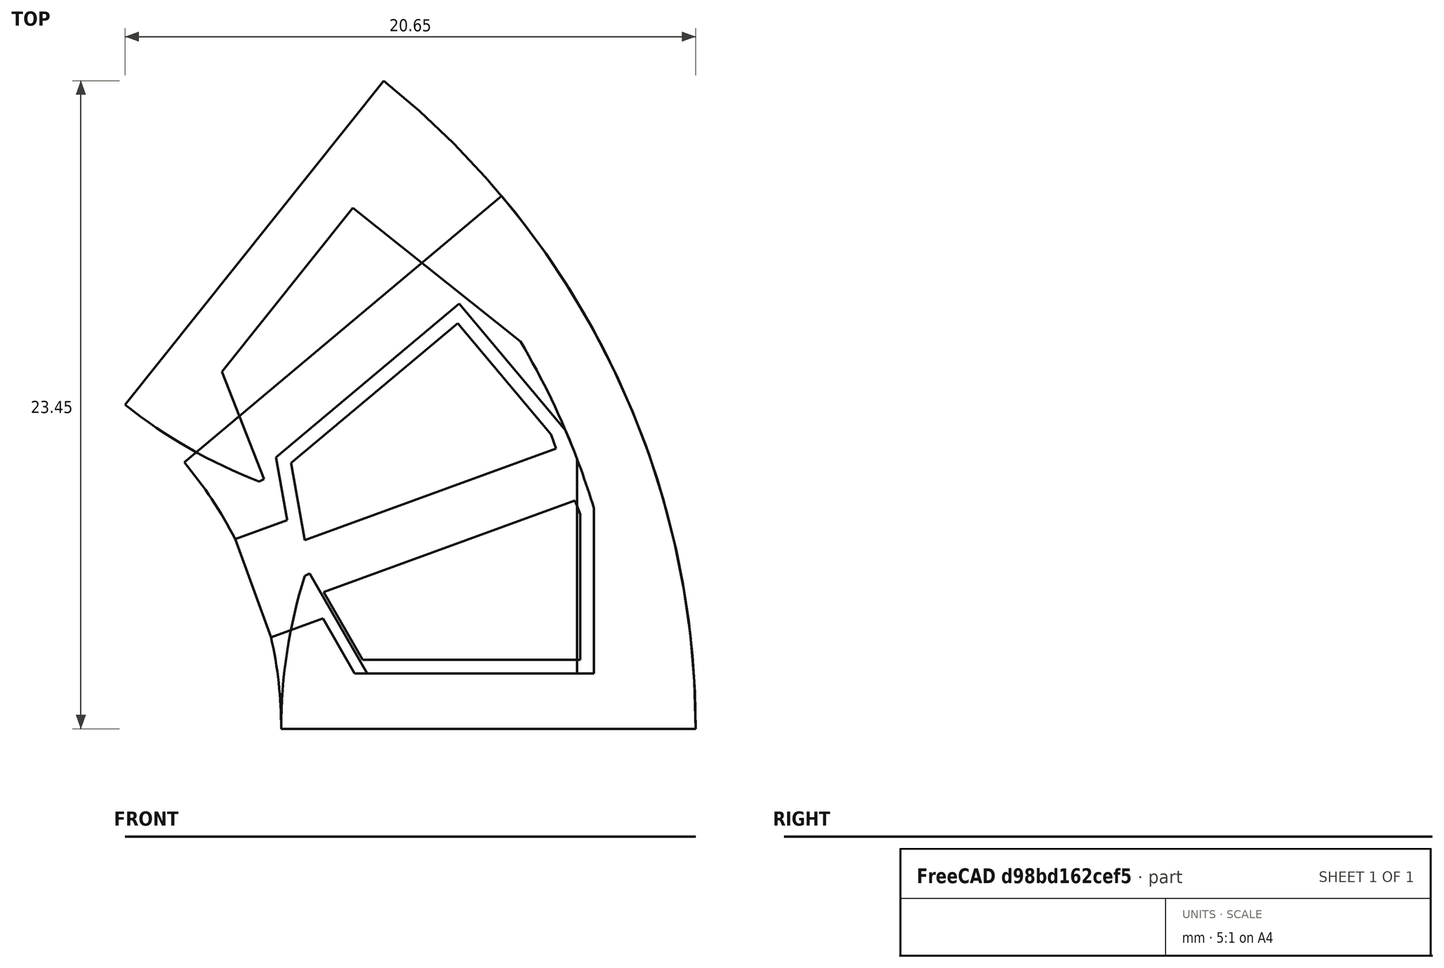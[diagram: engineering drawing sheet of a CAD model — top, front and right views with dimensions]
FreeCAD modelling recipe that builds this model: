
FCSTD DOCUMENT  (FreeCAD 0.18R4 (GitTag))
Label: StatorIRNeedleWinding
License: All rights reserved
LicenseURL: http://en.wikipedia.org/wiki/All_rights_reserved
objects: Sketcher::SketchObject×9, Surface::Filling×5, PartDesign::Body×2, Spreadsheet::Sheet×1
note: 16 computed .brp shape members not serialized (recipe doc carries the construction recipe); baked Part::Feature solids carry a one-line shape summary decoded from their .brp

FEATURE [Spreadsheet::Sheet] Spreadsheet  label="Variables"
  cells = A2=slotNumber; B2(slotNumber)=9; A3=outerDiameter; B3(outerDiameter)=60; A4=innerDiameter; B4(innerDiameter)=30; A5=stackLength; B5(stackLength)=20; A6=stackingFactor; B6(stackingFactor)=0.95; A7=cuttingThickness; B7(cuttingThickness)=0.1; A8=skewAngle; B8(skewAngle)=0; A9=segmentAngle; B9(segmentAngle)==360 / slotNumber; A10=tipHeightReduction; B10(tipHeightReduction)=0; A11=toothThickness; B11(toothThickness)=4; A12=yokeThickness; B12(yokeThickness)=2.5; A13=tipHeight; B13(tipHeight)=2; A14=tipAngle; B14(tipAngle)=120; A15=openingLeft; B15(openingLeft)=1.9; A16=openingRight; B16(openingRight)=1.9; A17=slotIsolation; B17(slotIsolation)=0.5; A18=windingAngle; B18(windingAngle)=35; A19=heightRatio; B19(heightRatio)=45; A20=roundingRadii; B20(roundingRadii)=0.2; A21=backWidth; B21(backWidth)=3; A22=backAngle; B22(backAngle)=90; A23=phaseSeparation; B23(phaseSeparation)=2; A24=axialOverhang; B24(axialOverhang)=1.2; A25=axialHeight; B25(axialHeight)=3
FEATURE [Sketcher::SketchObject] Sketch003  label="StatorSketch1"
  MapMode = 5
  Support = -> [XY_Plane]
  expr: Constraints[76] = Variables.backWidth
  expr: Constraints[37] = Variables.tipAngle
  expr: Constraints[60] = Variables.backAngle
  expr: Constraints[30] = Variables.tipHeight
  expr: Constraints[28] = Variables.openingRight
  expr: Constraints[32] = Variables.tipHeight * (1 - Variables.tipHeightReduction / 100)
  expr: Constraints[22] = Variables.openingLeft
  expr: Constraints[6] = Variables.outerDiameter / 2
  expr: Constraints[59] = Variables.tipHeight
  expr: Constraints[5] = Variables.segmentAngle
  expr: Constraints[11] = Variables.innerDiameter / 2
  expr: Constraints[54] = Variables.outerDiameter / 2 - Variables.yokeThickness
  expr: Constraints[49] = Variables.tipHeight * (1 - Variables.tipHeightReduction / 100)
  expr: Constraints[58] = Variables.toothThickness / 2
  expr: Constraints[18] = Variables.segmentAngle / 2
  expr: Constraints[50] = Variables.tipAngle
  expr: Constraints[52] = Variables.backAngle
  expr: Constraints[42] = Variables.toothThickness / 2
  sketch-geometry (27):
    g0: LineSegment [constr] StartX=0 StartY=0 StartZ=0 EndX=22.9813 EndY=19.2836 EndZ=0
    g1: LineSegment [constr] StartX=0 StartY=0 StartZ=0 EndX=30 EndY=0 EndZ=0
    g2: ArcOfCircle CenterX=0 CenterY=0 CenterZ=0 NormalX=0 NormalY=0 NormalZ=1 AngleXU=0 Radius=30 StartAngle=0 EndAngle=0.698132
    g3: ArcOfCircle [constr] CenterX=0 CenterY=0 CenterZ=0 NormalX=0 NormalY=0 NormalZ=1 AngleXU=0 Radius=15 StartAngle=0 EndAngle=0.698132
    g4: LineSegment [constr] StartX=13.3338 StartY=6.87098 StartZ=0 EndX=27.4859 EndY=12.0219 EndZ=0
    g5: LineSegment [constr] StartX=14.6308 StartY=3.30731 StartZ=0 EndX=28.7829 EndY=8.45826 EndZ=0
    g6: LineSegment [constr] StartX=28.1908 StartY=10.2606 StartZ=0 EndX=14.0954 EndY=5.1303 EndZ=0
    g7: LineSegment [constr] StartX=0 StartY=0 StartZ=0 EndX=14.0954 EndY=5.1303 EndZ=0
    g8: LineSegment [constr] StartX=13.3338 StartY=6.87098 StartZ=0 EndX=14.0954 EndY=5.1303 EndZ=0
    g9: LineSegment [constr] StartX=14.0954 StartY=5.1303 StartZ=0 EndX=14.6308 EndY=3.30731 EndZ=0
    g10: LineSegment [constr] StartX=13.3338 StartY=6.87098 StartZ=0 EndX=15.2132 EndY=7.55502 EndZ=0
    g11: LineSegment StartX=13.3338 StartY=6.87098 StartZ=0 EndX=15.2132 EndY=7.55502 EndZ=0
    g12: LineSegment StartX=15.2132 StartY=7.55502 StartZ=0 EndX=14.8139 EndY=9.8195 EndZ=0
    g13: LineSegment StartX=14.8139 StartY=9.8195 StartZ=0 EndX=21.4449 EndY=15.3836 EndZ=0
    g14: LineSegment [constr] StartX=14.8139 StartY=9.8195 StartZ=0 EndX=13.5283 EndY=11.3516 EndZ=0
    g15: LineSegment StartX=21.4449 StartY=15.3836 StartZ=0 EndX=25.29 EndY=10.8011 EndZ=0
    g16: LineSegment StartX=26.3161 StartY=7.98201 StartZ=0 EndX=26.3161 EndY=2 EndZ=0
    g17: LineSegment StartX=26.3161 StartY=2 StartZ=0 EndX=17.6599 EndY=2 EndZ=0
    g18: LineSegment StartX=17.6599 StartY=2 StartZ=0 EndX=16.5102 EndY=3.99135 EndZ=0
    g19: LineSegment StartX=16.5102 StartY=3.99135 StartZ=0 EndX=14.6308 EndY=3.30731 EndZ=0
    g20: LineSegment [constr] StartX=26.3161 StartY=2 StartZ=0 EndX=26.3161 EndY=0 EndZ=0
    g21: LineSegment StartX=11.4907 StartY=9.64181 StartZ=0 EndX=22.9813 EndY=19.2836 EndZ=0
    g22: LineSegment StartX=30 StartY=0 StartZ=0 EndX=15 EndY=0 EndZ=0
    g23: ArcOfCircle CenterX=4.23e-14 CenterY=0 CenterZ=0 NormalX=0 NormalY=0 NormalZ=1 AngleXU=0 Radius=15 StartAngle=0 EndAngle=0.222314
    g24: ArcOfCircle CenterX=-4.12e-14 CenterY=-3.45e-14 CenterZ=0 NormalX=0 NormalY=0 NormalZ=1 AngleXU=0 Radius=15 StartAngle=0.475817 EndAngle=0.698132
    g25: ArcOfCircle CenterX=0 CenterY=0 CenterZ=0 NormalX=0 NormalY=0 NormalZ=1 AngleXU=0 Radius=27.5 StartAngle=0.294493 EndAngle=0.403638
    g26: LineSegment [constr] StartX=25.29 StartY=10.8011 StartZ=0 EndX=26.3161 EndY=7.98201 EndZ=0
  constraints (77):
    c: Angle(g-1,g1) = 0
    c: Coincident(g0,g-1)
    c: Coincident(g1,g-1)
    c: Coincident(g2,g-1)
    c: Coincident(g2,g0)
    c: Angle(g1,g0) = 0.698132
    c: Radius(g2) = 30
    c: Coincident(g2,g1)
    c: Coincident(g3,g-1)
    c: PointOnObject(g3,g1)
    c: PointOnObject(g3,g0)
    c: Radius(g3) = 15
    c: PointOnObject(g4,g3)
    c: PointOnObject(g4,g2)
    c: PointOnObject(g5,g3)
    c: PointOnObject(g5,g2)
    c: PointOnObject(g6,g2)
    c: PointOnObject(g6,g3)
    c: Angle(g1,g6) = 0.349066
    c: Coincident(g7,g-1)
    c: Coincident(g7,g6)
    c: Coincident(g8,g4)
    c: Distance(g8) = 1.9
    c: Coincident(g8,g6)
    c: Parallel(g4,g6)
    c: Parallel(g5,g6)
    c: Coincident(g9,g6)
    c: Coincident(g9,g5)
    c: Distance(g9) = 1.9
    c: PointOnObject(g10,g4)
    c: Distance(g4,g10) = 2
    c: Angle(g4,g10) = 3.14159
    c: Distance(g10,g10) = 2
    c: Coincident(g11,g10)
    c: Coincident(g12,g11)
    c: Coincident(g13,g12)
    c: Coincident(g11,g10)
    c: Angle(g12,g13) = 2.0944
    c: Parallel(g0,g13)
    c: Coincident(g14,g12)
    c: PointOnObject(g14,g0)
    c: Angle(g13,g14) = 1.5708
    c: Distance(g14) = 2
    c: Coincident(g15,g13)
    c: Coincident(g17,g16)
    c: Coincident(g18,g17)
    c: PointOnObject(g18,g5)
    c: Coincident(g19,g18)
    c: PointOnObject(g19,g5)
    c: Distance(g19) = 2
    c: Angle(g17,g18) = 2.0944
    c: Parallel(g17,g1)
    c: Angle(g16,g17) = 1.5708
    c: Symmetric(g15,g16,g6)
    c: Distance(g-1,g15) = 27.5
    c: Coincident(g20,g16)
    c: PointOnObject(g20,g1)
    c: Vertical(g20)
    c: DistanceY(g20,g20) = 2
    c: Distance(g5,g18) = 2
    c: Angle(g13,g15) = 1.5708
    c: Coincident(g21,g3)
    c: Coincident(g21,g0)
    c: Coincident(g22,g2)
    c: Coincident(g22,g3)
    c: PointOnObject(g23,g-1)
    c: Coincident(g23,g19)
    c: Coincident(g23,g22)
    c: PointOnObject(g24,g0)
    c: Coincident(g24,g11)
    c: Coincident(g24,g21)
    c: Coincident(g25,g2)
    c: Coincident(g25,g15)
    c: Coincident(g25,g16)
    c: Coincident(g26,g15)
    c: Coincident(g26,g16)
    c: Distance(g26) = 3
FEATURE [Sketcher::SketchObject] Sketch  label="StatorStack"
  MapMode = 5
  Support = -> [XY_Plane001]
  expr: Constraints[20] = Variables.innerDiameter / 2
  expr: Constraints[10] = Variables.outerDiameter / 2
  expr: Constraints[9] = Variables.innerDiameter / 2
  expr: Constraints[8] = Variables.stackLength
  sketch-geometry (8):
    g0: LineSegment StartX=-10 StartY=15 StartZ=0 EndX=10 EndY=15 EndZ=0
    g1: LineSegment StartX=10 StartY=15 StartZ=0 EndX=10 EndY=30 EndZ=0
    g2: LineSegment StartX=10 StartY=30 StartZ=0 EndX=-10 EndY=30 EndZ=0
    g3: LineSegment StartX=-10 StartY=30 StartZ=0 EndX=-10 EndY=15 EndZ=0
    g4: LineSegment StartX=-10 StartY=-15 StartZ=0 EndX=10 EndY=-15 EndZ=0
    g5: LineSegment StartX=10 StartY=-15 StartZ=0 EndX=10 EndY=-30 EndZ=0
    g6: LineSegment StartX=10 StartY=-30 StartZ=0 EndX=-10 EndY=-30 EndZ=0
    g7: LineSegment StartX=-10 StartY=-30 StartZ=0 EndX=-10 EndY=-15 EndZ=0
  constraints (22):
    c: Coincident(g0,g1)
    c: Coincident(g1,g2)
    c: Coincident(g2,g3)
    c: Coincident(g3,g0)
    c: Horizontal(g2)
    c: Vertical(g1)
    c: Vertical(g3)
    c: Symmetric(g0,g0,g-2)
    c: DistanceX(g0,g0) = 20
    c: DistanceY(g-1,g0) = 15
    c: DistanceY(g-1,g1) = 30
    c: Coincident(g4,g5)
    c: Coincident(g5,g6)
    c: Coincident(g6,g7)
    c: Coincident(g7,g4)
    c: Horizontal(g6)
    c: Vertical(g5)
    c: Vertical(g7)
    c: Equal(g4,g0)
    c: Symmetric(g4,g4,g-2)
    c: DistanceY(g4,g-1) = 15
    c: Equal(g7,g3)
FEATURE [Sketcher::SketchObject] Sketch005  label="StatorSketch2"
  MapMode = 5
  Support = -> [XY_Plane]
  expr: Constraints[76] = Variables.backWidth
  expr: Constraints[51] = Variables.tipAngle
  expr: Constraints[28] = Variables.openingRight
  expr: Constraints[30] = Variables.tipHeight
  expr: Constraints[37] = Variables.tipAngle
  expr: Constraints[60] = Variables.tipHeight
  expr: Constraints[32] = Variables.tipHeight * (1 - Variables.tipHeightReduction / 100)
  expr: Constraints[61] = Variables.backAngle
  expr: Constraints[6] = Variables.outerDiameter / 2
  expr: Constraints[5] = Variables.segmentAngle
  expr: Constraints[22] = Variables.openingLeft
  expr: Constraints[55] = Variables.outerDiameter / 2 - Variables.yokeThickness
  expr: Constraints[59] = Variables.toothThickness / 2
  expr: Constraints[50] = Variables.tipHeight * (1 - Variables.tipHeightReduction / 100)
  expr: Constraints[18] = Variables.segmentAngle / 2
  expr: Constraints[11] = Variables.innerDiameter / 2
  expr: Constraints[53] = Variables.backAngle
  expr: Constraints[42] = Variables.toothThickness / 2
  sketch-geometry (27):
    g0: LineSegment [constr] StartX=0 StartY=0 StartZ=0 EndX=18.7047 EndY=23.4549 EndZ=0
    g1: LineSegment [constr] StartX=0 StartY=0 StartZ=0 EndX=30 EndY=0 EndZ=0
    g2: ArcOfCircle CenterX=0 CenterY=0 CenterZ=0 NormalX=0 NormalY=0 NormalZ=1 AngleXU=0 Radius=30 StartAngle=0 EndAngle=0.897598
    g3: ArcOfCircle [constr] CenterX=0 CenterY=0 CenterZ=0 NormalX=0 NormalY=0 NormalZ=1 AngleXU=0 Radius=15 StartAngle=0 EndAngle=0.897598
    g4: LineSegment [constr] StartX=12.5834 StartY=8.16445 StartZ=0 EndX=26.1523 EndY=14.6989 EndZ=0
    g5: LineSegment [constr] StartX=14.2288 StartY=4.74764 StartZ=0 EndX=27.7977 EndY=11.2821 EndZ=0
    g6: LineSegment [constr] StartX=27.0291 StartY=13.0165 StartZ=0 EndX=13.5145 EndY=6.50826 EndZ=0
    g7: LineSegment [constr] StartX=0 StartY=0 StartZ=0 EndX=13.5145 EndY=6.50826 EndZ=0
    g8: LineSegment [constr] StartX=12.5834 StartY=8.16445 StartZ=0 EndX=13.5145 EndY=6.50826 EndZ=0
    g9: LineSegment [constr] StartX=13.5145 StartY=6.50826 StartZ=0 EndX=14.2288 EndY=4.74764 EndZ=0
    g10: LineSegment [constr] StartX=14.2051 StartY=8.94544 StartZ=0 EndX=14.3853 EndY=9.03222 EndZ=0
    g11: LineSegment StartX=14.2051 StartY=8.94544 StartZ=0 EndX=14.3853 EndY=9.03222 EndZ=0
    g12: LineSegment StartX=14.3853 StartY=9.03222 StartZ=0 EndX=12.8601 EndY=12.9183 EndZ=0
    g13: LineSegment StartX=12.8601 StartY=12.9183 StartZ=0 EndX=17.5931 EndY=18.8533 EndZ=0
    g14: LineSegment [constr] StartX=12.8601 StartY=12.9183 StartZ=0 EndX=11.2965 EndY=14.1653 EndZ=0
    g15: LineSegment StartX=17.5931 StartY=18.8533 StartZ=0 EndX=23.6613 EndY=14.0141 EndZ=0
    g16: LineSegment [constr] StartX=23.6613 StartY=14.0141 StartZ=0 EndX=25.7092 EndY=9.7615 EndZ=0
    g17: LineSegment StartX=25.7092 StartY=9.7615 StartZ=0 EndX=25.7092 EndY=2 EndZ=0
    g18: LineSegment StartX=25.7092 StartY=2 StartZ=0 EndX=18.1181 EndY=2 EndZ=0
    g19: LineSegment StartX=18.1181 StartY=2 StartZ=0 EndX=16.0308 EndY=5.61541 EndZ=0
    g20: LineSegment StartX=16.0308 StartY=5.61541 StartZ=0 EndX=15.8506 EndY=5.52863 EndZ=0
    g21: LineSegment [constr] StartX=25.7092 StartY=2 StartZ=0 EndX=25.7092 EndY=0 EndZ=0
    g22: LineSegment StartX=9.35235 StartY=11.7275 StartZ=0 EndX=18.7047 EndY=23.4549 EndZ=0
    g23: LineSegment StartX=30 StartY=0 StartZ=0 EndX=15 EndY=0 EndZ=0
    g24: ArcOfCircle CenterX=20.8201 CenterY=26.1075 CenterZ=0 NormalX=0 NormalY=0 NormalZ=1 AngleXU=0 Radius=18.3928 StartAngle=4.03919 EndAngle=4.3445
    g25: ArcOfCircle CenterX=33.3928 CenterY=0 CenterZ=0 NormalX=0 NormalY=0 NormalZ=1 AngleXU=0 Radius=18.3928 StartAngle=2.83628 EndAngle=3.14159
    g26: ArcOfCircle CenterX=0 CenterY=0 CenterZ=0 NormalX=0 NormalY=0 NormalZ=1 AngleXU=0 Radius=27.5 StartAngle=0.362875 EndAngle=0.534723
  constraints (77):
    c: Angle(g-1,g1) = 0
    c: Coincident(g0,g-1)
    c: Coincident(g1,g-1)
    c: Coincident(g2,g-1)
    c: Coincident(g2,g0)
    c: Angle(g1,g0) = 0.698132
    c: Radius(g2) = 30
    c: Coincident(g2,g1)
    c: Coincident(g3,g-1)
    c: PointOnObject(g3,g1)
    c: PointOnObject(g3,g0)
    c: Radius(g3) = 15
    c: PointOnObject(g4,g3)
    c: PointOnObject(g4,g2)
    c: PointOnObject(g5,g3)
    c: PointOnObject(g5,g2)
    c: PointOnObject(g6,g2)
    c: PointOnObject(g6,g3)
    c: Angle(g1,g6) = 0.349066
    c: Coincident(g7,g-1)
    c: Coincident(g7,g6)
    c: Coincident(g8,g4)
    c: Distance(g8) = 1.9
    c: Coincident(g8,g6)
    c: Parallel(g4,g6)
    c: Parallel(g5,g6)
    c: Coincident(g9,g6)
    c: Coincident(g9,g5)
    c: Distance(g9) = 1.9
    c: PointOnObject(g10,g4)
    c: Distance(g4,g10) = 2
    c: Angle(g4,g10) = 3.14159
    c: Distance(g10,g10) = 2
    c: Coincident(g11,g10)
    c: Coincident(g12,g11)
    c: Coincident(g13,g12)
    c: Coincident(g11,g10)
    c: Angle(g12,g13) = 2.0944
    c: Parallel(g0,g13)
    c: Coincident(g14,g12)
    c: PointOnObject(g14,g0)
    c: Angle(g13,g14) = 1.5708
    c: Distance(g14) = 2
    c: Coincident(g15,g13)
    c: Coincident(g16,g15)
    c: Coincident(g17,g16)
    c: Coincident(g18,g17)
    c: Coincident(g19,g18)
    c: PointOnObject(g19,g5)
    c: Coincident(g20,g19)
    c: Distance(g20) = 2
    c: Angle(g18,g19) = 2.0944
    c: Parallel(g18,g1)
    c: Angle(g17,g18) = 1.5708
    c: Symmetric(g15,g16,g6)
    c: Distance(g-1,g15) = 27.5
    c: Coincident(g21,g17)
    c: PointOnObject(g21,g1)
    c: Vertical(g21)
    c: DistanceY(g21,g21) = 2
    c: Distance(g5,g19) = 2
    c: Angle(g13,g15) = 1.5708
    c: Coincident(g22,g3)
    c: Coincident(g22,g0)
    c: Coincident(g23,g2)
    c: Coincident(g23,g3)
    c: PointOnObject(g24,g22)
    c: Coincident(g24,g11)
    c: Coincident(g24,g22)
    c: Angle(g5,g20) = 3.14159
    c: PointOnObject(g25,g-1)
    c: Coincident(g25,g20)
    c: Coincident(g25,g23)
    c: Coincident(g26,g2)
    c: Coincident(g26,g15)
    c: Coincident(g26,g17)
    c: Distance(g16) = 3
FEATURE [Sketcher::SketchObject] Sketch008  label="SlotSketch"
  MapMode = 5
  Support = -> [XY_Plane]
  expr: Constraints[50] = Variables.toothThickness / 2
  expr: Constraints[18] = Variables.segmentAngle / 2
  expr: Constraints[30] = Variables.tipAngle
  expr: Constraints[51] = Variables.tipHeight
  expr: Constraints[28] = Variables.openingRight
  expr: Constraints[67] = Variables.backWidth
  expr: Constraints[46] = Variables.outerDiameter / 2 - Variables.yokeThickness
  expr: Constraints[22] = Variables.openingLeft
  expr: Constraints[6] = Variables.outerDiameter / 2
  expr: Constraints[44] = Variables.backAngle
  expr: Constraints[52] = Variables.backAngle
  expr: Constraints[11] = Variables.innerDiameter / 2
  expr: Constraints[5] = Variables.segmentAngle
  expr: Constraints[42] = Variables.tipAngle
  expr: Constraints[35] = Variables.toothThickness / 2
  sketch-geometry (25):
    g0: LineSegment [constr] StartX=0 StartY=0 StartZ=0 EndX=22.9813 EndY=19.2836 EndZ=0
    g1: LineSegment [constr] StartX=0 StartY=0 StartZ=0 EndX=30 EndY=0 EndZ=0
    g2: ArcOfCircle [constr] CenterX=0 CenterY=0 CenterZ=0 NormalX=0 NormalY=0 NormalZ=1 AngleXU=0 Radius=30 StartAngle=0 EndAngle=0.698132
    g3: ArcOfCircle [constr] CenterX=0 CenterY=0 CenterZ=0 NormalX=0 NormalY=0 NormalZ=1 AngleXU=0 Radius=15 StartAngle=0 EndAngle=0.698132
    g4: LineSegment [constr] StartX=13.3338 StartY=6.87098 StartZ=0 EndX=27.4859 EndY=12.0219 EndZ=0
    g5: LineSegment [constr] StartX=14.6308 StartY=3.30731 StartZ=0 EndX=28.7829 EndY=8.45826 EndZ=0
    g6: LineSegment [constr] StartX=28.1908 StartY=10.2606 StartZ=0 EndX=14.0954 EndY=5.1303 EndZ=0
    g7: LineSegment [constr] StartX=0 StartY=0 StartZ=0 EndX=14.0954 EndY=5.1303 EndZ=0
    g8: LineSegment [constr] StartX=13.3338 StartY=6.87098 StartZ=0 EndX=14.0954 EndY=5.1303 EndZ=0
    g9: LineSegment [constr] StartX=14.0954 StartY=5.1303 StartZ=0 EndX=14.6308 EndY=3.30731 EndZ=0
    g10: LineSegment StartX=15.2132 StartY=7.55502 StartZ=0 EndX=14.8139 EndY=9.8195 EndZ=0
    g11: LineSegment StartX=14.8139 StartY=9.8195 StartZ=0 EndX=21.4449 EndY=15.3836 EndZ=0
    g12: LineSegment [constr] StartX=14.8139 StartY=9.8195 StartZ=0 EndX=13.5283 EndY=11.3516 EndZ=0
    g13: LineSegment StartX=21.4449 StartY=15.3836 StartZ=0 EndX=25.29 EndY=10.8011 EndZ=0
    g14: LineSegment [constr] StartX=25.29 StartY=10.8011 StartZ=0 EndX=26.3161 EndY=7.98201 EndZ=0
    g15: LineSegment StartX=26.3161 StartY=7.98201 StartZ=0 EndX=26.3161 EndY=2 EndZ=0
    g16: LineSegment StartX=26.3161 StartY=2 StartZ=0 EndX=17.6599 EndY=2 EndZ=0
    g17: LineSegment StartX=17.6599 StartY=2 StartZ=0 EndX=16.5102 EndY=3.99135 EndZ=0
    g18: LineSegment [constr] StartX=26.3161 StartY=2 StartZ=0 EndX=26.3161 EndY=0 EndZ=0
    g19: LineSegment [constr] StartX=11.4907 StartY=9.64181 StartZ=0 EndX=22.9813 EndY=19.2836 EndZ=0
    g20: LineSegment [constr] StartX=30 StartY=0 StartZ=0 EndX=15 EndY=0 EndZ=0
    g21: LineSegment StartX=13.3338 StartY=6.87098 StartZ=0 EndX=14.6308 EndY=3.30731 EndZ=0
    g22: LineSegment StartX=13.3338 StartY=6.87098 StartZ=0 EndX=15.2132 EndY=7.55502 EndZ=0
    g23: LineSegment StartX=14.6308 StartY=3.30731 StartZ=0 EndX=16.5102 EndY=3.99135 EndZ=0
    g24: ArcOfCircle CenterX=0 CenterY=0 CenterZ=0 NormalX=0 NormalY=0 NormalZ=1 AngleXU=0 Radius=27.5 StartAngle=0.294493 EndAngle=0.403638
  constraints (68):
    c: Angle(g-1,g1) = 0
    c: Coincident(g0,g-1)
    c: Coincident(g1,g-1)
    c: Coincident(g2,g-1)
    c: Coincident(g2,g0)
    c: Angle(g1,g0) = 0.698132
    c: Radius(g2) = 30
    c: Coincident(g2,g1)
    c: Coincident(g3,g-1)
    c: PointOnObject(g3,g1)
    c: PointOnObject(g3,g0)
    c: Radius(g3) = 15
    c: PointOnObject(g4,g3)
    c: PointOnObject(g4,g2)
    c: PointOnObject(g5,g3)
    c: PointOnObject(g5,g2)
    c: PointOnObject(g6,g2)
    c: PointOnObject(g6,g3)
    c: Angle(g1,g6) = 0.349066
    c: Coincident(g7,g-1)
    c: Coincident(g7,g6)
    c: Coincident(g8,g4)
    c: Distance(g8) = 1.9
    c: Coincident(g8,g6)
    c: Parallel(g4,g6)
    c: Parallel(g5,g6)
    c: Coincident(g9,g6)
    c: Coincident(g9,g5)
    c: Distance(g9) = 1.9
    c: Coincident(g11,g10)
    c: Angle(g10,g11) = 2.0944
    c: Parallel(g0,g11)
    c: Coincident(g12,g10)
    c: PointOnObject(g12,g0)
    c: Angle(g11,g12) = 1.5708
    c: Distance(g12) = 2
    c: Coincident(g13,g11)
    c: Coincident(g14,g13)
    c: Coincident(g15,g14)
    c: Coincident(g16,g15)
    c: Coincident(g17,g16)
    c: PointOnObject(g17,g5)
    c: Angle(g16,g17) = 2.0944
    c: Parallel(g16,g1)
    c: Angle(g15,g16) = 1.5708
    c: Symmetric(g13,g14,g6)
    c: Distance(g-1,g13) = 27.5
    c: Coincident(g18,g15)
    c: PointOnObject(g18,g1)
    c: Vertical(g18)
    c: DistanceY(g18,g18) = 2
    c: Distance(g5,g17) = 2
    c: Angle(g11,g13) = 1.5708
    c: Coincident(g19,g3)
    c: Coincident(g19,g0)
    c: Coincident(g20,g2)
    c: Coincident(g20,g3)
    c: Symmetric(g17,g10,g6)
    c: Coincident(g21,g4)
    c: Coincident(g21,g5)
    c: Coincident(g22,g21)
    c: Coincident(g22,g10)
    c: Coincident(g23,g21)
    c: Coincident(g23,g17)
    c: Coincident(g24,g-1)
    c: Coincident(g24,g13)
    c: Coincident(g24,g15)
    c: Distance(g14) = 3
FEATURE [Sketcher::SketchObject] Sketch006  label="TerminalLeftSketch"
  ExternalGeometry = -> [Sketch008]
  MapMode = 5
  Support = -> [XY_Plane]
  expr: Constraints[28] = abs(Variables.backWidth - Variables.phaseSeparation) / 2 + Variables.slotIsolation / 15
  expr: Constraints[21] = Variables.slotIsolation
  expr: Constraints[14] = Variables.phaseSeparation / 2
  sketch-geometry (10):
    g0: LineSegment StartX=24.7672 StartY=10.6463 StartZ=0 EndX=21.3833 EndY=14.6792 EndZ=0
    g1: LineSegment StartX=21.3833 StartY=14.6792 StartZ=0 EndX=15.3564 EndY=9.62204 EndZ=0
    g2: LineSegment StartX=15.3564 StartY=9.62204 StartZ=0 EndX=15.8483 EndY=6.83248 EndZ=0
    g3: LineSegment StartX=15.8483 StartY=6.83248 StartZ=0 EndX=24.9497 EndY=10.1451 EndZ=0
    g4: LineSegment StartX=24.9497 StartY=10.1451 StartZ=0 EndX=24.7672 EndY=10.6463 EndZ=0
    g5: LineSegment [constr] StartX=0 StartY=0 StartZ=0 EndX=15.8617 EndY=5.77319 EndZ=0
    g6: LineSegment [constr] StartX=15.8483 StartY=6.83248 StartZ=0 EndX=16.1903 EndY=5.89279 EndZ=0
    g7: LineSegment [constr] StartX=21.3833 StartY=14.6792 StartZ=0 EndX=21.7663 EndY=15.0006 EndZ=0
    g8: LineSegment [constr] StartX=21.3833 StartY=14.6792 StartZ=0 EndX=21.0619 EndY=15.0622 EndZ=0
    g9: LineSegment [constr] StartX=15.3564 StartY=9.62204 StartZ=0 EndX=14.864 EndY=9.53521 EndZ=0
  constraints (29):
    c: Coincident(g1,g0)
    c: Coincident(g2,g1)
    c: Coincident(g3,g2)
    c: Coincident(g4,g3)
    c: Coincident(g4,g0)
    c: Parallel(g1,g-4)
    c: Parallel(g-5,g2)
    c: Parallel(g0,g-3)
    c: Angle(g4,g3) = 1.5708
    c: Symmetric(g-5,g-6,g5)
    c: Parallel(g3,g5)
    c: Coincident(g6,g2)
    c: PointOnObject(g6,g5)
    c: Angle(g6,g5) = 1.5708
    c: Distance(g6) = 1
    c: Coincident(g7,g0)
    c: PointOnObject(g7,g-3)
    c: Coincident(g8,g0)
    c: PointOnObject(g8,g-4)
    c: Angle(g0,g7) = 1.5708
    c: Angle(g8,g1) = 1.5708
    c: Distance(g8) = 0.5
    c: Equal(g8,g7)
    c: Coincident(g5,g-1)
    c: Coincident(g9,g1)
    c: PointOnObject(g9,g-5)
    c: Angle(g-5,g9) = 1.5708
    c: Equal(g8,g9)
    c: Distance(g4) = 0.533333
FEATURE [Sketcher::SketchObject] Sketch007  label="TerminalRightSketch"
  ExternalGeometry = -> [Sketch008]
  MapMode = 5
  Support = -> [XY_Plane]
  expr: Constraints[27] = Variables.slotIsolation
  expr: Constraints[26] = abs(Variables.backWidth - Variables.phaseSeparation) / 2 + Variables.slotIsolation / 15
  expr: Constraints[13] = Variables.phaseSeparation / 2
  sketch-geometry (10):
    g0: LineSegment [constr] StartX=0 StartY=0 StartZ=0 EndX=15.8617 EndY=5.77319 EndZ=0
    g1: LineSegment StartX=25.8161 StartY=7.76456 StartZ=0 EndX=25.8161 EndY=2.5 EndZ=0
    g2: LineSegment StartX=25.8161 StartY=2.5 StartZ=0 EndX=17.9486 EndY=2.5 EndZ=0
    g3: LineSegment StartX=17.9486 StartY=2.5 StartZ=0 EndX=16.5323 EndY=4.95309 EndZ=0
    g4: LineSegment StartX=16.5323 StartY=4.95309 StartZ=0 EndX=25.6337 EndY=8.26572 EndZ=0
    g5: LineSegment StartX=25.6337 StartY=8.26572 StartZ=0 EndX=25.8161 EndY=7.76456 EndZ=0
    g6: LineSegment [constr] StartX=16.5323 StartY=4.95309 StartZ=0 EndX=16.1903 EndY=5.89279 EndZ=0
    g7: LineSegment [constr] StartX=25.8161 StartY=2.5 StartZ=0 EndX=25.8161 EndY=2 EndZ=0
    g8: LineSegment [constr] StartX=25.8161 StartY=2.5 StartZ=0 EndX=26.3161 EndY=2.5 EndZ=0
    g9: LineSegment [constr] StartX=17.9486 StartY=2.5 StartZ=0 EndX=17.5156 EndY=2.25 EndZ=0
  constraints (29):
    c: Symmetric(g-5,g-6,g0)
    c: Coincident(g0,g-1)
    c: Vertical(g1)
    c: Coincident(g2,g1)
    c: Horizontal(g2)
    c: Coincident(g3,g2)
    c: Coincident(g4,g3)
    c: Coincident(g5,g4)
    c: Coincident(g5,g1)
    c: Parallel(g0,g4)
    c: Coincident(g6,g3)
    c: PointOnObject(g6,g0)
    c: Angle(g0,g6) = 1.5708
    c: Distance(g6) = 1
    c: Angle(g4,g5) = 1.5708
    c: Coincident(g7,g1)
    c: PointOnObject(g7,g-7)
    c: Coincident(g8,g1)
    c: PointOnObject(g8,g-8)
    c: Angle(g8,g1) = 1.5708
    c: Angle(g2,g7) = 1.5708
    c: Equal(g8,g7)
    c: Parallel(g3,g-6)
    c: Coincident(g9,g2)
    c: PointOnObject(g9,g-6)
    c: Angle(g3,g9) = 1.5708
    c: Distance(g5) = 0.533333
    c: Distance(g8) = 0.5
    c: Equal(g8,g9)
FEATURE [Surface::Filling] Surface  label="SlotSketch_Surface"
  Anisotropy = false
  BoundaryEdges = -> [Sketch008]
  BoundaryOrder = [0,0,0,0,0,0,0,0,0,0]
  Degree = 3
  Iterations = 2
  MaximumDegree = 8
  MaximumSegments = 9
  PointsOnCurve = 15
  TolAngular = 0.01
  TolCurvature = 0.1
  Tolerance2d = 1e-05
  Tolerance3d = 0.0001
FEATURE [Surface::Filling] Surface001  label="StatorSketch2_Surface"
  Anisotropy = false
  BoundaryEdges = -> [Sketch005]
  BoundaryOrder = [0,0,0,0,0,0,0,0,0,0,0,0,0,0]
  Degree = 3
  Iterations = 2
  MaximumDegree = 8
  MaximumSegments = 9
  PointsOnCurve = 15
  TolAngular = 0.01
  TolCurvature = 0.1
  Tolerance2d = 1e-05
  Tolerance3d = 0.0001
FEATURE [Surface::Filling] Surface002  label="StatorSketch1_Surface"
  Anisotropy = false
  BoundaryEdges = -> [Sketch003]
  BoundaryOrder = [0,0,0,0,0,0,0,0,0,0,0,0,0,0]
  Degree = 3
  Iterations = 2
  MaximumDegree = 8
  MaximumSegments = 9
  PointsOnCurve = 15
  TolAngular = 0.01
  TolCurvature = 0.1
  Tolerance2d = 1e-05
  Tolerance3d = 0.0001
FEATURE [Surface::Filling] Surface003  label="TerminalRightSketch_Surface"
  Anisotropy = false
  BoundaryEdges = -> [Sketch007]
  BoundaryOrder = [0,0,0,0,0]
  Degree = 3
  Iterations = 2
  MaximumDegree = 8
  MaximumSegments = 9
  PointsOnCurve = 15
  TolAngular = 0.01
  TolCurvature = 0.1
  Tolerance2d = 1e-05
  Tolerance3d = 0.0001
FEATURE [Surface::Filling] Surface004  label="TerminalLeftSketch_Surface"
  Anisotropy = false
  BoundaryEdges = -> [Sketch006]
  BoundaryOrder = [0,0,0,0,0]
  Degree = 3
  Iterations = 2
  MaximumDegree = 8
  MaximumSegments = 9
  PointsOnCurve = 15
  TolAngular = 0.01
  TolCurvature = 0.1
  Tolerance2d = 1e-05
  Tolerance3d = 0.0001
FEATURE [Sketcher::SketchObject] Sketch010  label="ToothLine"
  ExternalGeometry = -> [Sketch008]
  MapMode = 5
  Support = -> [XY_Plane]
  expr: Constraints[0] = Variables.toothThickness
  sketch-geometry (1):
    g0: LineSegment StartX=18.1294 StartY=12.6015 StartZ=0 EndX=15.5582 EndY=15.6657 EndZ=0
  constraints (3):
    c: Distance(g0) = 4
    c: Symmetric(g-3,g-3,g0)
    c: Angle(g-3,g0) = 1.5708
FEATURE [Sketcher::SketchObject] Sketch011  label="YokeLine"
  ExternalGeometry = -> [Sketch008]
  MapMode = 5
  Support = -> [XY_Plane]
  expr: Constraints[7] = Variables.outerDiameter / 2
  sketch-geometry (3):
    g0: LineSegment [constr] StartX=25.29 StartY=10.8011 StartZ=0 EndX=26.3161 EndY=7.98201 EndZ=0
    g1: LineSegment StartX=25.8415 StartY=9.40555 StartZ=0 EndX=28.1908 EndY=10.2606 EndZ=0
    g2: LineSegment [constr] StartX=25.8415 StartY=9.40555 StartZ=0 EndX=25.8031 EndY=9.39155 EndZ=0
  constraints (8):
    c: Coincident(g2,g1)
    c: Angle(g0,g2) = 1.5708
    c: Symmetric(g0,g0,g2)
    c: Parallel(g2,g1)
    c: Coincident(g0,g-3)
    c: Coincident(g0,g-3)
    c: PointOnObject(g1,g-3)
    c: Distance(g-1,g1) = 30
FEATURE [PartDesign::Body] Body  label="TopView"
  Group = -> [Sketch003,Sketch005,Sketch006,Sketch007,Sketch008,Sketch010,Sketch011]
  Origin = -> Origin
FEATURE [Sketcher::SketchObject] Sketch012  label="Isolation"
  ExternalGeometry = -> [Sketch]
  MapMode = 5
  Support = -> [XY_Plane001]
  expr: Constraints[75] = Variables.axialHeight / 2
  expr: Constraints[9] = Variables.axialHeight + Variables.axialOverhang
  expr: Constraints[10] = Variables.axialHeight
  expr: Constraints[13] = (Variables.outerDiameter - Variables.innerDiameter) / 2 - Variables.yokeThickness - Variables.tipHeight
  expr: Constraints[12] = Variables.yokeThickness
  expr: Constraints[11] = Variables.tipHeight
  sketch-geometry (32):
    g0: LineSegment StartX=-10 StartY=30 StartZ=0 EndX=-10 EndY=15 EndZ=0
    g1: LineSegment StartX=-10 StartY=15 StartZ=0 EndX=-12.7 EndY=15 EndZ=0
    g2: LineSegment StartX=-12.7 StartY=15 StartZ=0 EndX=-12.7 EndY=17 EndZ=0
    g3: LineSegment StartX=-12.7 StartY=17 StartZ=0 EndX=-11.2 EndY=17 EndZ=0
    g4: LineSegment StartX=-11.2 StartY=17 StartZ=0 EndX=-11.2 EndY=27.5 EndZ=0
    g5: LineSegment StartX=-11.2 StartY=27.5 StartZ=0 EndX=-14.2 EndY=27.5 EndZ=0
    g6: LineSegment StartX=-14.2 StartY=27.5 StartZ=0 EndX=-14.2 EndY=30 EndZ=0
    g7: LineSegment StartX=-14.2 StartY=30 StartZ=0 EndX=-10 EndY=30 EndZ=0
    g8: LineSegment StartX=-12.7 StartY=-15 StartZ=0 EndX=-10 EndY=-15 EndZ=0
    g9: LineSegment StartX=-10 StartY=-15 StartZ=0 EndX=-10 EndY=-30 EndZ=0
    g10: LineSegment StartX=-10 StartY=-30 StartZ=0 EndX=-14.2 EndY=-30 EndZ=0
    g11: LineSegment StartX=-14.2 StartY=-30 StartZ=0 EndX=-14.2 EndY=-27.5 EndZ=0
    g12: LineSegment StartX=-14.2 StartY=-27.5 StartZ=0 EndX=-11.2 EndY=-27.5 EndZ=0
    g13: LineSegment StartX=-11.2 StartY=-27.5 StartZ=0 EndX=-11.2 EndY=-17 EndZ=0
    g14: LineSegment StartX=-11.2 StartY=-17 StartZ=0 EndX=-12.7 EndY=-17 EndZ=0
    g15: LineSegment StartX=-12.7 StartY=-17 StartZ=0 EndX=-12.7 EndY=-15 EndZ=0
    g16: LineSegment StartX=14.2 StartY=30 StartZ=0 EndX=10 EndY=30 EndZ=0
    g17: LineSegment StartX=10 StartY=30 StartZ=0 EndX=10 EndY=15 EndZ=0
    g18: LineSegment StartX=10 StartY=15 StartZ=0 EndX=12.7 EndY=15 EndZ=0
    g19: LineSegment StartX=12.7 StartY=15 StartZ=0 EndX=12.7 EndY=17 EndZ=0
    g20: LineSegment StartX=12.7 StartY=17 StartZ=0 EndX=11.2 EndY=17 EndZ=0
    g21: LineSegment StartX=11.2 StartY=17 StartZ=0 EndX=11.2 EndY=27.5 EndZ=0
    g22: LineSegment StartX=11.2 StartY=27.5 StartZ=0 EndX=14.2 EndY=27.5 EndZ=0
    g23: LineSegment StartX=14.2 StartY=27.5 StartZ=0 EndX=14.2 EndY=30 EndZ=0
    g24: LineSegment StartX=12.7 StartY=-15 StartZ=0 EndX=10 EndY=-15 EndZ=0
    g25: LineSegment StartX=10 StartY=-15 StartZ=0 EndX=10 EndY=-30 EndZ=0
    g26: LineSegment StartX=10 StartY=-30 StartZ=0 EndX=14.2 EndY=-30 EndZ=0
    g27: LineSegment StartX=14.2 StartY=-30 StartZ=0 EndX=14.2 EndY=-27.5 EndZ=0
    g28: LineSegment StartX=14.2 StartY=-27.5 StartZ=0 EndX=11.2 EndY=-27.5 EndZ=0
    g29: LineSegment StartX=11.2 StartY=-27.5 StartZ=0 EndX=11.2 EndY=-17 EndZ=0
    g30: LineSegment StartX=11.2 StartY=-17 StartZ=0 EndX=12.7 EndY=-17 EndZ=0
    g31: LineSegment StartX=12.7 StartY=-17 StartZ=0 EndX=12.7 EndY=-15 EndZ=0
  constraints (91):
    c: Coincident(g1,g0)
    c: Coincident(g2,g1)
    c: Coincident(g3,g2)
    c: Coincident(g4,g3)
    c: Vertical(g4)
    c: Coincident(g5,g4)
    c: Coincident(g7,g6)
    c: Coincident(g7,g0)
    c: Coincident(g6,g5)
    c: DistanceX(g7,g7) = 4.2
    c: DistanceX(g5,g5) = 3
    c: DistanceY(g2,g2) = 2
    c: DistanceY(g6,g6) = 2.5
    c: DistanceY(g4,g4) = 10.5
    c: Coincident(g0,g-6)
    c: Coincident(g8,g9)
    c: Vertical(g9)
    c: Coincident(g9,g10)
    c: Coincident(g10,g11)
    c: Coincident(g11,g12)
    c: Coincident(g12,g13)
    c: Vertical(g13)
    c: Coincident(g13,g14)
    c: Coincident(g14,g15)
    c: Coincident(g15,g8)
    c: Equal(g7,g10)
    c: Vertical(g11)
    c: Equal(g13,g4)
    c: Equal(g9,g0)
    c: Equal(g11,g6)
    c: Coincident(g8,g-4)
    c: Coincident(g16,g17)
    c: Vertical(g17)
    c: Coincident(g17,g18)
    c: Coincident(g18,g19)
    c: Coincident(g19,g20)
    c: Coincident(g20,g21)
    c: Vertical(g21)
    c: Coincident(g21,g22)
    c: Coincident(g22,g23)
    c: Coincident(g23,g16)
    c: Equal(g0,g17)
    c: Equal(g16,g7)
    c: Equal(g2,g19)
    c: Equal(g6,g23)
    c: Coincident(g-3,g16)
    c: Coincident(g24,g25)
    c: Vertical(g25)
    c: Coincident(g25,g26)
    c: Coincident(g26,g27)
    c: Vertical(g27)
    c: Coincident(g27,g28)
    c: Coincident(g28,g29)
    c: Vertical(g29)
    c: Coincident(g29,g30)
    c: Coincident(g30,g31)
    c: Coincident(g31,g24)
    c: Equal(g8,g24)
    c: Equal(g10,g26)
    c: Equal(g11,g27)
    c: Equal(g15,g31)
    c: Equal(g9,g25)
    c: Coincident(g24,g-5)
    c: Angle(g17,g16) = 1.5708
    c: Angle(g21,g22) = 1.5708
    c: Angle(g18,g17) = 1.5708
    c: Angle(g20,g21) = 1.5708
    c: Angle(g25,g24) = 1.5708
    c: Angle(g29,g30) = 1.5708
    c: Angle(g28,g29) = 1.5708
    c: Angle(g26,g25) = 1.5708
    c: Angle(g14,g13) = 1.5708
    c: Angle(g13,g12) = 1.5708
    c: Angle(g9,g10) = 1.5708
    c: Angle(g8,g9) = 1.5708
    c: DistanceX(g3,g3) = 1.5
    c: Angle(g6,g7) = 1.5708
    c: Equal(g20,g3)
    c: Equal(g3,g14)
    c: Angle(g15,g8) = 1.5708
    c: Equal(g12,g5)
    c: Equal(g28,g5)
    c: Equal(g5,g22)
    c: Angle(g24,g31) = 1.5708
    c: Angle(g19,g18) = 1.5708
    c: Angle(g23,g22) = 1.5708
    c: Angle(g5,g4) = 1.5708
    c: Coincident(g0,g-6)
    c: Angle(g1,g2) = 1.5708
    c: Angle(g7,g0) = 1.5708
    c: Angle(g0,g1) = 1.5708
FEATURE [PartDesign::Body] Body001  label="SideView"
  Group = -> [Sketch,Sketch012]
  Origin = -> Origin001
